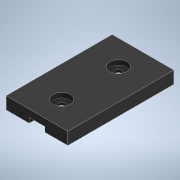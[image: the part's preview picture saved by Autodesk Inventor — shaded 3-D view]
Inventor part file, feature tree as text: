
AUTODESK INVENTOR PART (.ipt)
format: ipt  version: 2021 (Build 250183000, 183)  size: 128,000 bytes
history: native  units: mm
features: extrude x3, sketch x3
ambient origin geometry x8: Origin, YZ Plane, XZ Plane, XY Plane, X Axis, Y Axis, Z Axis, Center Point
bodies: Solid1 (feature_tree)
feature tree (6):
  extrude  "Extrusion1"  Depth=2.0mm
  extrude  "Extrusion2"  Depth=5.0mm
  extrude  "Extrusion3"  Depth=2.5mm
  sketch  "Sketch1"  dims[d0=3.2mm d1=2.0mm]
  sketch  "Sketch2"  dims[d2=9.3mm d3=5.0mm]
  sketch  "Sketch3"  dims[d4=43.0mm d5=0.0mm d6=2.5mm d7=2.5mm d8=10.0mm d9=10.0mm d10=43.0mm d11=0.0mm d12=7.0mm d13=7.0mm d14=2.0mm d15=0.0mm]
